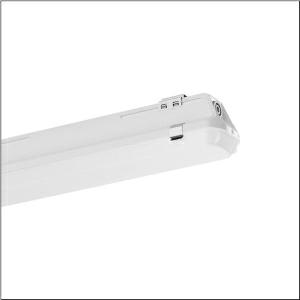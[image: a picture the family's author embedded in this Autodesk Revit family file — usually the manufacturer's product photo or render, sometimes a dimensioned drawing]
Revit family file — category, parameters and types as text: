
# Revit family: monsun_r__11_51fp10mp480h_5fdf
name_source: partatom
category: Lighting Fixtures
units: mm (PartAtom-declared; Revit-internal decimal feet)

## family parameters
Cut with Voids When Loaded = No
Host = Face
Light Source = No
Part Type = Normal
Room Calculation Point = No
Round Connector Dimension = Use Diameter
Shared = No

## types (1)
- --- (1 x LED, 8070 lm, 45.4 W, 4000K)
    Apparent Load = 45 VA
    CIE Flux Codes = 47 77 93 94 100
    Color Rendering = 80
    Color Temperature = 4000K
    Default Elevation = 1800 mm
    Description = Monsun® 11, damp-proof luminaire, chain hanger, primary optical cover: enclosure, of PMMA, light emission: direct distribution, primary light characteristic: symmetric, installation type: suspended mounting, surface-mounted, horizontal mounting, vertical mounting, LED, rated luminous flux: 8.070lm, luminous efficacy: 178lm/W, light colour: 840, colour temperature: 4000K, control gear: ECG, with terminal, 3-pole, max. 2.5mm², mains connection: 220..240V, AC, 50/60Hz, rated input power: 45W, luminaire housing, of glass-fibre reinforced polyester, uncoated, bright grey, incl. chain hanger, length: 1.590mm, width: 90mm, height: 88mm, clip for enclosure, of stainless steel (V2A), ceiling mounting element, of stainless steel (V2A), chain hanger, of stainless steel (V2A), protection rating (complete): IP66, insulation class (complete): insulation class I (protective earthing), certification: CE, ENEC, VDE, UKCA, protection symbol: D, impact resistance: IK04, permissible operating ambient temperature: -35..+40°C, standard: EN 50419, EN 60598-2-1, no direct snow, no direct sun, no direct rain, for indoor or canopied outdoor use, corresponds to IFS (International Featured Standards) requirements for safety and quality in the food industry, contact your sales advisor before using the luminaires in applications with unclear chemical exposure, large temperature fluctuations or condensation-forming humidity, LABS conformity tested according to VDMA 24364:2018-05, packaging unit: 1 piece
    Height = 89 mm
    Lamp = 1 x LED
    Lamp Light Flux = 8070 lm
    Lamp Power = 45.4 W
    Lamp count = 1
    Length = 1590 mm
    Luminous efficacy = 178 lm/W
    Manufacturer = Siteco
    ModVariant = No
    Model = 51FP10MP480H
    Mounting Place = Ceiling
    Mounting Type = Surface mounted
    Number of Poles = 1
    OnlyDefault = Yes
    Power Factor = 1
    Product Name = Monsun® 11
    Product group = damp-proof luminaire
    ProductGroupID = 300
    Protection Class = Protection class I
    Protection Degree = IP 66
    RLX_Detail_Level = 1
    RLX_Emergency_Light_Flux = 0 lm
    RLX_Emergency_Type = 0
    RLX_Emergency_Type_DB = No
    RlxData = <blob elided: 89809 chars, md5=58a79ec3>
    Socket = socket
    Standby Power = 0 W
    System Light Flux = 8070 lm
    System Power = 45 W
    Type Comments = factory setting: luminous flux: 100 % | (A | C | E) | 105 mA
    Type Image = l_1004748.jpg
    URL = http://relux.com
    VarID = @adj_142493
    Voltage = 0 V
    Weight = 0.00 kg
    Width = 90 mm

## geometry (parser evidence)
native form markers: Blend x4, Sweep x14
no freeform markers — native parametric forms only
